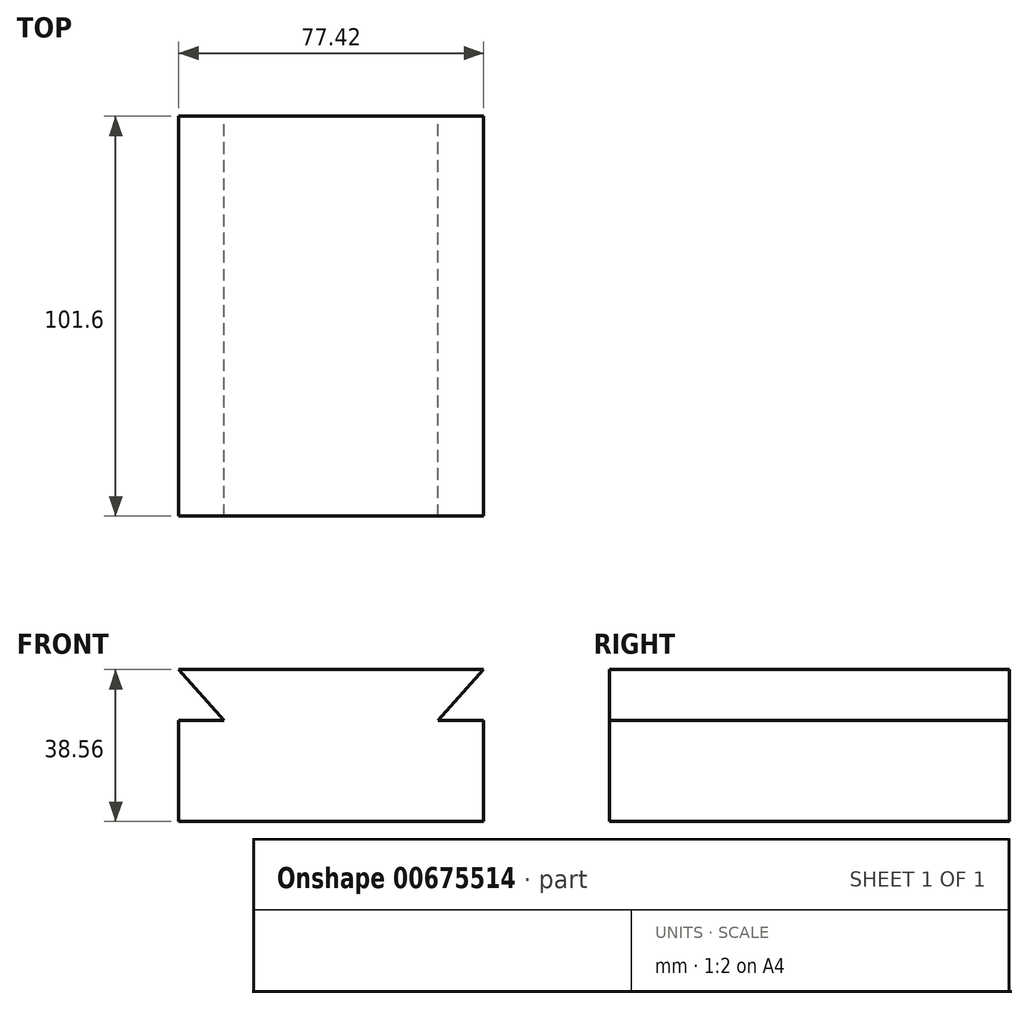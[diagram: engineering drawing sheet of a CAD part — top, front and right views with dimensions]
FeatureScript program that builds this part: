
annotation { "Feature Type Name" : "Feature", "Feature Type Description" : "" }
export const myFeature = defineFeature(function(context is Context, id is Id, definition is map)
    precondition{}
    {
        {
            var Q0;
            Q0=qCreatedBy(makeId("Front.planeOp"),FACE);
            var sketch = newSketch(context, id + "F0", { "sketchPlane" : qUnion([Q0])});
            skLineSegment(sketch, "E0", {"start": v(-31.51, 24.03) * mm, "end": v(45.9, 24.03) * mm});
            skLineSegment(sketch, "E1", {"start": v(45.9, 24.03) * mm, "end": v(34.4, 11.08) * mm});
            skLineSegment(sketch, "E2", {"start": v(34.4, 11.08) * mm, "end": v(45.9, 11.08) * mm});
            skLineSegment(sketch, "E3", {"start": v(45.9, 11.08) * mm, "end": v(45.9, -14.53) * mm});
            skLineSegment(sketch, "E4", {"start": v(45.9, -14.53) * mm, "end": v(-31.51, -14.53) * mm});
            skLineSegment(sketch, "E5", {"start": v(-31.51, -14.53) * mm, "end": v(-31.51, 11.08) * mm});
            skLineSegment(sketch, "E6", {"start": v(-31.51, 11.08) * mm, "end": v(-20, 11.08) * mm});
            skLineSegment(sketch, "E7", {"start": v(-20, 11.08) * mm, "end": v(-31.51, 24.03) * mm});
            skSolve(sketch);
        }
        {
            var Q0;
            Q0 = qSketchRegion(id + "F0", true);
            extrude(context, id + "F1", {"entities" : qUnion([Q0]), "depth" : 101.6 * mm, "offsetDistance" : 25.4 * mm});
        }
    });
